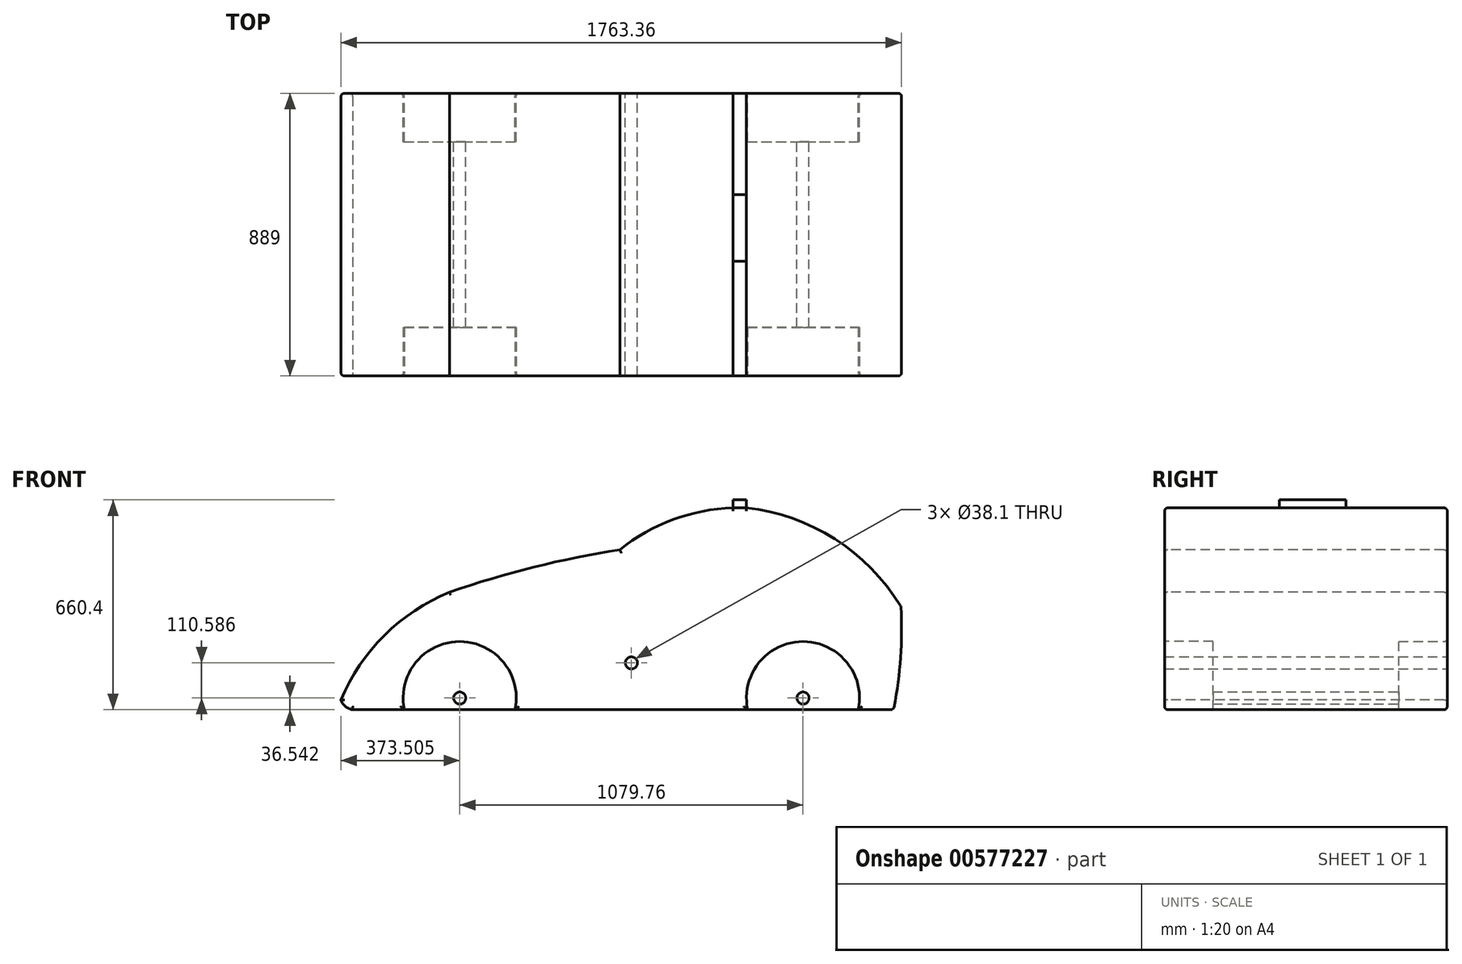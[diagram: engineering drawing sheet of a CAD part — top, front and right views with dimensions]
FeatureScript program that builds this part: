
annotation { "Feature Type Name" : "Feature", "Feature Type Description" : "" }
export const myFeature = defineFeature(function(context is Context, id is Id, definition is map)
    precondition{}
    {
        {
            var Q0;
            Q0=qCreatedBy(makeId("Top.planeOp"),FACE);
            var sketch = newSketch(context, id + "F0", { "sketchPlane" : qUnion([Q0])});
            skLineSegment(sketch, "E0.bottom", {"start": v(-1258.23, 428.51) * mm, "end": v(519.77, 428.51) * mm});
            skLineSegment(sketch, "E0.top", {"start": v(-1258.23, -460.49) * mm, "end": v(519.77, -460.49) * mm});
            skLineSegment(sketch, "E0.left", {"start": v(-1258.23, 428.51) * mm, "end": v(-1258.23, -460.49) * mm});
            skLineSegment(sketch, "E0.right", {"start": v(519.77, 428.51) * mm, "end": v(519.77, -460.49) * mm});
            skSolve(sketch);
        }
        {
            var Q0;
            Q0=makeQuery(id+"F0.imprint","IMPRINT",FACE,{"disambiguationData":[TD([[makeQuery(id+"F0.imprint","IMPRINT",EDGE,{"derivedFrom":sQuery(id+"F0.wireOp",EDGE,"E0.bottom")}),-1.0]])]});
            extrude(context, id + "F1", {"entities" : qUnion([Q0]), "depth" : 635 * mm, "offsetDistance" : 25.4 * mm});
        }
        {
            var Q0;
            Q0=makeQuery(id+"F1.opExtrude","SWEPT_FACE",FACE,{"disambiguationData":[OSD([sQuery(id+"F0.wireOp",EDGE,"E0.top")])]});
            var sketch = newSketch(context, id + "F2", { "sketchPlane" : qUnion([Q0])});
            skLineSegment(sketch, "E1.bottom", {"start": v(-369.23, 0) * mm, "end": v(519.77, 0) * mm});
            skLineSegment(sketch, "E1.top", {"start": v(-369.23, 635) * mm, "end": v(519.77, 635) * mm});
            skLineSegment(sketch, "E1.left", {"start": v(-369.23, 0) * mm, "end": v(-369.23, 635) * mm});
            skLineSegment(sketch, "E1.right", {"start": v(519.77, 0) * mm, "end": v(519.77, 635) * mm});
            skArc(sketch, "E2", {"start": v(-369.23, 502.85) * mm, "mid": v(-824.62, 396.46) * mm, "end": v(-1258.23, 221.32) * mm});
            skArc(sketch, "E3", {"start": v(25.9, 635) * mm, "mid": v(-183.55, 604.47) * mm, "end": v(-369.23, 502.85) * mm});
            skArc(sketch, "E4", {"start": v(519.77, 408) * mm, "mid": v(299.94, 580.46) * mm, "end": v(25.9, 635) * mm});
            skArc(sketch, "E5", {"start": v(-905.03, 369.75) * mm, "mid": v(-1121.06, 222.54) * mm, "end": v(-1258.23, 0) * mm});
            skArc(sketch, "E6", {"start": v(-1246.6, 30.18) * mm, "mid": v(-1227.53, 6.34) * mm, "end": v(-1197.67, 0) * mm});
            skSolve(sketch);
        }
        {
            var Q0;
            {var subQ0=sQuery(id+"F2.wireOp",EDGE,"E1.right");var subQ1=sQuery(id+"F2.wireOp",EDGE,"E1.top");var subQ2=makeQuery(id+"F2.imprint","INTERSECT",VERTEX,{"derivedFrom":[subQ1,subQ0]});Q0=makeQuery(id+"F2.imprint","IMPRINT",FACE,{"disambiguationData":[TD([[makeQuery(id+"F2.imprint","IMPRINT",EDGE,{"disambiguationData":[TD([[subQ2,1.0]])],"derivedFrom":subQ1}),-1.0]])]});}
            var Q1;
            {var subQ3=sQuery(id+"F2.wireOp",EDGE,"E3");Q1=makeQuery(id+"F2.imprint","IMPRINT",FACE,{"disambiguationData":[TD([[makeQuery(id+"F2.imprint","IMPRINT",EDGE,{"derivedFrom":subQ3}),-1.0]])]});}
            var Q2;
            {var subQ4=sQuery(id+"F2.wireOp",EDGE,"E2");Q2=makeQuery(id+"F2.imprint","IMPRINT",FACE,{"disambiguationData":[TD([[makeQuery(id+"F2.imprint","IMPRINT",EDGE,{"derivedFrom":subQ4}),-1.0]])]});}
            extrude(context, id + "F3", {"entities" : qUnion([Q0, Q1, Q2]), "operationType" : NewBodyOperationType.REMOVE, "oppositeDirection" : true, "depth" : 889 * mm, "offsetDistance" : 25.4 * mm});
        }
        {
            var Q0;
            Q0=makeQuery(id+"F1.opExtrude","SWEPT_FACE",FACE,{"disambiguationData":[OSD([sQuery(id+"F0.wireOp",EDGE,"E0.top")])]});
            var sketch = newSketch(context, id + "F4", { "sketchPlane" : qUnion([Q0])});
            skArc(sketch, "E7", {"start": v(491.3, 0) * mm, "mid": v(516.19, 212.78) * mm, "end": v(504.3, 426.68) * mm});
            skArc(sketch, "E8", {"start": v(514.57, 324.76) * mm, "mid": v(307.8, 536.4) * mm, "end": v(28.82, 635) * mm});
            skArc(sketch, "E9", {"start": v(-1118.04, 286.56) * mm, "mid": v(-1221.3, 159.5) * mm, "end": v(-1258.23, 0) * mm});
            skArc(sketch, "E10", {"start": v(441.78, 0) * mm, "mid": v(471.92, 10.65) * mm, "end": v(497.13, 30.28) * mm});
            skSolve(sketch);
        }
        {
            var Q0;
            {var subQ0=sQuery(id+"F4.wireOp",EDGE,"E7");Q0=makeQuery(id+"F4.imprint","IMPRINT",FACE,{"disambiguationData":[TD([[makeQuery(id+"F4.imprint","IMPRINT",EDGE,{"derivedFrom":subQ0}),-1.0]])]});}
            extrude(context, id + "F5", {"entities" : qUnion([Q0]), "operationType" : NewBodyOperationType.REMOVE, "oppositeDirection" : true, "depth" : 889 * mm, "offsetDistance" : 25.4 * mm});
        }
        {
            var Q0;
            {var subQ3=sQuery(id+"F4.wireOp",EDGE,"E8");Q0=makeQuery(id+"F4.imprint","IMPRINT",FACE,{"disambiguationData":[TD([[makeQuery(id+"F4.imprint","IMPRINT",EDGE,{"derivedFrom":subQ3}),-1.0]])]});}
            extrude(context, id + "F6", {"entities" : qUnion([Q0]), "operationType" : NewBodyOperationType.REMOVE, "oppositeDirection" : true, "depth" : 889 * mm, "offsetDistance" : 25.4 * mm});
        }
        {
            var Q0;
            {var subQ4=sQuery(id+"F2.wireOp",EDGE,"E5");Q0=makeQuery(id+"F2.imprint","IMPRINT",FACE,{"disambiguationData":[TD([[makeQuery(id+"F2.imprint","IMPRINT",EDGE,{"derivedFrom":subQ4}),-1.0]])]});}
            extrude(context, id + "F7", {"entities" : qUnion([Q0]), "operationType" : NewBodyOperationType.REMOVE, "oppositeDirection" : true, "depth" : 889 * mm, "offsetDistance" : 25.4 * mm});
        }
        {
            var Q0;
            {var subQ0=sQuery(id+"F2.wireOp",EDGE,"E5");var subQ4=sQuery(id+"F2.wireOp",EDGE,"E6");var subQ5=makeQuery(id+"F2.imprint","INTERSECT",VERTEX,{"derivedFrom":[subQ0,subQ4]});Q0=makeQuery(id+"F2.imprint","IMPRINT",FACE,{"disambiguationData":[TD([[makeQuery(id+"F2.imprint","IMPRINT",EDGE,{"disambiguationData":[TD([[subQ5,-1.0]])],"derivedFrom":subQ4}),-1.0]])]});}
            extrude(context, id + "F8", {"entities" : qUnion([Q0]), "operationType" : NewBodyOperationType.REMOVE, "oppositeDirection" : true, "depth" : 889 * mm, "offsetDistance" : 25.4 * mm});
        }
        {
            var Q0;
            Q0=makeQuery(id+"F1.opExtrude","SWEPT_FACE",FACE,{"disambiguationData":[OSD([sQuery(id+"F0.wireOp",EDGE,"E0.top")])]});
            var sketch = newSketch(context, id + "F9", { "sketchPlane" : qUnion([Q0])});
            skCircle(sketch, "E11", {"center": v(-873.09, 36.54) * mm, "radius": 177.8 * mm});
            skCircle(sketch, "E12", {"center": v(206.68, 36.54) * mm, "radius": 177.8 * mm});
            skSolve(sketch);
        }
        {
            var Q0;
            {var subQ0=sQuery(id+"F9.wireOp",EDGE,"E12");var subQ1=makeQuery(id+"F1.opExtrude","CAP_EDGE",EDGE,{"disambiguationData":[OSD([sQuery(id+"F0.wireOp",EDGE,"E0.top")])],"isStart":true});var subQ2=makeQuery(id+"F9.imprint","INTERSECT",VERTEX,{"disambiguationData":[OD(0.0)],"derivedFrom":[subQ1,subQ0]});Q0=makeQuery(id+"F9.imprint","IMPRINT",FACE,{"disambiguationData":[TD([[makeQuery(id+"F9.imprint","IMPRINT",EDGE,{"disambiguationData":[TD([[subQ2,-1.0]])],"derivedFrom":subQ0}),1.0]])]});}
            var Q1;
            {var subQ0=sQuery(id+"F9.wireOp",EDGE,"E11");var subQ1=makeQuery(id+"F1.opExtrude","CAP_EDGE",EDGE,{"disambiguationData":[OSD([sQuery(id+"F0.wireOp",EDGE,"E0.top")])],"isStart":true});var subQ2=makeQuery(id+"F9.imprint","INTERSECT",VERTEX,{"disambiguationData":[OD(0.0)],"derivedFrom":[subQ1,subQ0]});Q1=makeQuery(id+"F9.imprint","IMPRINT",FACE,{"disambiguationData":[TD([[makeQuery(id+"F9.imprint","IMPRINT",EDGE,{"disambiguationData":[TD([[subQ2,1.0]])],"derivedFrom":subQ0}),1.0]])]});}
            extrude(context, id + "F10", {"entities" : qUnion([Q0, Q1]), "operationType" : NewBodyOperationType.REMOVE, "oppositeDirection" : true, "depth" : 152.4 * mm, "offsetDistance" : 25.4 * mm});
        }
        {
            var Q0;
            Q0=makeQuery(id+"F1.opExtrude","SWEPT_FACE",FACE,{"disambiguationData":[OSD([sQuery(id+"F0.wireOp",EDGE,"E0.bottom")])]});
            var sketch = newSketch(context, id + "F11", { "sketchPlane" : qUnion([Q0])});
            skCircle(sketch, "E13.0", {"center": v(-206.68, 36.54) * mm, "radius": 177.8 * mm});
            skCircle(sketch, "E14.0", {"center": v(873.09, 36.54) * mm, "radius": 177.8 * mm});
            skCircle(sketch, "E15", {"center": v(873.09, 36.54) * mm, "radius": 19.05 * mm});
            skCircle(sketch, "E16", {"center": v(-206.68, 36.54) * mm, "radius": 19.05 * mm});
            skSolve(sketch);
        }
        {
            var Q0;
            Q0=makeQuery(id+"F11.imprint","IMPRINT",FACE,{"disambiguationData":[TD([[makeQuery(id+"F11.imprint","IMPRINT",EDGE,{"derivedFrom":sQuery(id+"F11.wireOp",EDGE,"E15")}),1.0]])]});
            extrude(context, id + "F12", {"entities" : qUnion([Q0]), "operationType" : NewBodyOperationType.REMOVE, "oppositeDirection" : true, "depth" : 812.8 * mm, "offsetDistance" : 25.4 * mm});
        }
        {
            var Q0;
            Q0=makeQuery(id+"F11.imprint","IMPRINT",FACE,{"disambiguationData":[TD([[makeQuery(id+"F11.imprint","IMPRINT",EDGE,{"derivedFrom":sQuery(id+"F11.wireOp",EDGE,"E15")}),-1.0]])]});
            extrude(context, id + "F13", {"entities" : qUnion([Q0]), "operationType" : NewBodyOperationType.REMOVE, "oppositeDirection" : true, "depth" : 152.4 * mm, "offsetDistance" : 25.4 * mm});
        }
        {
            var Q0;
            Q0=makeQuery(id+"F11.imprint","IMPRINT",FACE,{"disambiguationData":[TD([[makeQuery(id+"F11.imprint","IMPRINT",EDGE,{"derivedFrom":sQuery(id+"F11.wireOp",EDGE,"E16")}),1.0]])]});
            extrude(context, id + "F14", {"entities" : qUnion([Q0]), "operationType" : NewBodyOperationType.REMOVE, "oppositeDirection" : true, "depth" : 609.6 * mm, "offsetDistance" : 25.4 * mm});
        }
        {
            var Q0;
            Q0=makeQuery(id+"F11.imprint","IMPRINT",FACE,{"disambiguationData":[TD([[makeQuery(id+"F11.imprint","IMPRINT",EDGE,{"derivedFrom":sQuery(id+"F11.wireOp",EDGE,"E16")}),-1.0]])]});
            extrude(context, id + "F15", {"entities" : qUnion([Q0]), "operationType" : NewBodyOperationType.REMOVE, "oppositeDirection" : true, "depth" : 152.4 * mm, "offsetDistance" : 25.4 * mm});
        }
        {
            var Q0;
            Q0=makeQuery(id+"F11.imprint","IMPRINT",FACE,{"disambiguationData":[TD([[makeQuery(id+"F11.imprint","IMPRINT",EDGE,{"derivedFrom":sQuery(id+"F11.wireOp",EDGE,"E16")}),1.0]])]});
            extrude(context, id + "F16", {"entities" : qUnion([Q0]), "operationType" : NewBodyOperationType.REMOVE, "oppositeDirection" : true, "depth" : 863.6 * mm, "offsetDistance" : 25.4 * mm});
        }
        {
            var Q0;
            {var subQ0=sQuery(id+"F9.wireOp",EDGE,"E11");var subQ1=makeQuery(id+"F1.opExtrude","CAP_EDGE",EDGE,{"disambiguationData":[OSD([sQuery(id+"F0.wireOp",EDGE,"E0.top")])],"isStart":true});var subQ2=makeQuery(id+"F9.imprint","INTERSECT",VERTEX,{"disambiguationData":[OD(0.0)],"derivedFrom":[subQ1,subQ0]});Q0=makeQuery(id+"F9.imprint","IMPRINT",FACE,{"disambiguationData":[TD([[makeQuery(id+"F9.imprint","IMPRINT",EDGE,{"disambiguationData":[TD([[subQ2,1.0]])],"derivedFrom":subQ0}),1.0]])]});}
            var Q1;
            {var subQ0=sQuery(id+"F9.wireOp",EDGE,"E12");var subQ1=makeQuery(id+"F1.opExtrude","CAP_EDGE",EDGE,{"disambiguationData":[OSD([sQuery(id+"F0.wireOp",EDGE,"E0.top")])],"isStart":true});var subQ2=makeQuery(id+"F9.imprint","INTERSECT",VERTEX,{"disambiguationData":[OD(0.0)],"derivedFrom":[subQ1,subQ0]});Q1=makeQuery(id+"F9.imprint","IMPRINT",FACE,{"disambiguationData":[TD([[makeQuery(id+"F9.imprint","IMPRINT",EDGE,{"disambiguationData":[TD([[subQ2,-1.0]])],"derivedFrom":subQ0}),1.0]])]});}
            extrude(context, id + "F17", {"entities" : qUnion([Q0, Q1]), "operationType" : NewBodyOperationType.REMOVE, "oppositeDirection" : true, "depth" : 152.4 * mm, "offsetDistance" : 25.4 * mm});
        }
        {
            var Q0;
            Q0=makeQuery(id+"F1.opExtrude","SWEPT_FACE",FACE,{"disambiguationData":[OSD([sQuery(id+"F0.wireOp",EDGE,"E0.top")])]});
            var Q1;
            Q1=makeQuery(id+"F5.boolean.opBoolean","COPY",FACE,{"derivedFrom":makeQuery(id+"F5.opExtrude","SWEPT_FACE",FACE,{"disambiguationData":[OSD([sQuery(id+"F4.wireOp",EDGE,"E7")])]})});
            var Q2;
            Q2=makeQuery(id+"F1.opExtrude","SWEPT_FACE",FACE,{"disambiguationData":[OSD([sQuery(id+"F0.wireOp",EDGE,"E0.bottom")])]});
            fillet(context, id + "F18", {"entities" : qUnion([Q0, Q1, Q2]), "radius" : 10.16 * mm, "tangentPropagation" : true, "allowEdgeOverflow" : false});
        }
        {
            var Q0;
            Q0=makeQuery(id+"F1.opExtrude","SWEPT_FACE",FACE,{"disambiguationData":[OSD([sQuery(id+"F0.wireOp",EDGE,"E0.bottom")])]});
            var sketch = newSketch(context, id + "F19", { "sketchPlane" : qUnion([Q0])});
            skCircle(sketch, "E17", {"center": v(333.2, 147.13) * mm, "radius": 19.05 * mm});
            skPoint(sketch, "E17.centerSnap0", {"position": v(333.2, 10.16) * mm});
            skSolve(sketch);
        }
        {
            var Q0;
            Q0 = qSketchRegion(id + "F19", true);
            extrude(context, id + "F20", {"entities" : qUnion([Q0]), "operationType" : NewBodyOperationType.REMOVE, "oppositeDirection" : true, "depth" : 889 * mm, "offsetDistance" : 25.4 * mm});
        }
        {
            var Q0;
            Q0=makeQuery(id+"F1.opExtrude","CAP_FACE",FACE,{"disambiguationData":[OSD([sQuery(id+"F0.wireOp",EDGE,"E0.bottom"),sQuery(id+"F0.wireOp",EDGE,"E0.top"),sQuery(id+"F0.wireOp",EDGE,"E0.left"),sQuery(id+"F0.wireOp",EDGE,"E0.right")])],"isStart":false});
            var sketch = newSketch(context, id + "F21", { "sketchPlane" : qUnion([Q0])});
            skLineSegment(sketch, "E18.bottom", {"start": v(28.82, 109.75) * mm, "end": v(-13.9, 109.75) * mm});
            skLineSegment(sketch, "E18.top", {"start": v(28.82, -99.2) * mm, "end": v(-13.9, -99.2) * mm});
            skLineSegment(sketch, "E18.left", {"start": v(28.82, 109.75) * mm, "end": v(28.82, -99.2) * mm});
            skLineSegment(sketch, "E18.right", {"start": v(-13.9, 109.75) * mm, "end": v(-13.9, -99.2) * mm});
            skSolve(sketch);
        }
        {
            var Q0;
            Q0=makeQuery(id+"F21.imprint","IMPRINT",FACE,{"disambiguationData":[TD([[makeQuery(id+"F21.imprint","IMPRINT",EDGE,{"derivedFrom":sQuery(id+"F21.wireOp",EDGE,"E18.bottom")}),1.0]])]});
            extrude(context, id + "F22", {"entities" : qUnion([Q0]), "operationType" : NewBodyOperationType.ADD, "depth" : 25.4 * mm, "offsetDistance" : 25.4 * mm});
        }
    });
